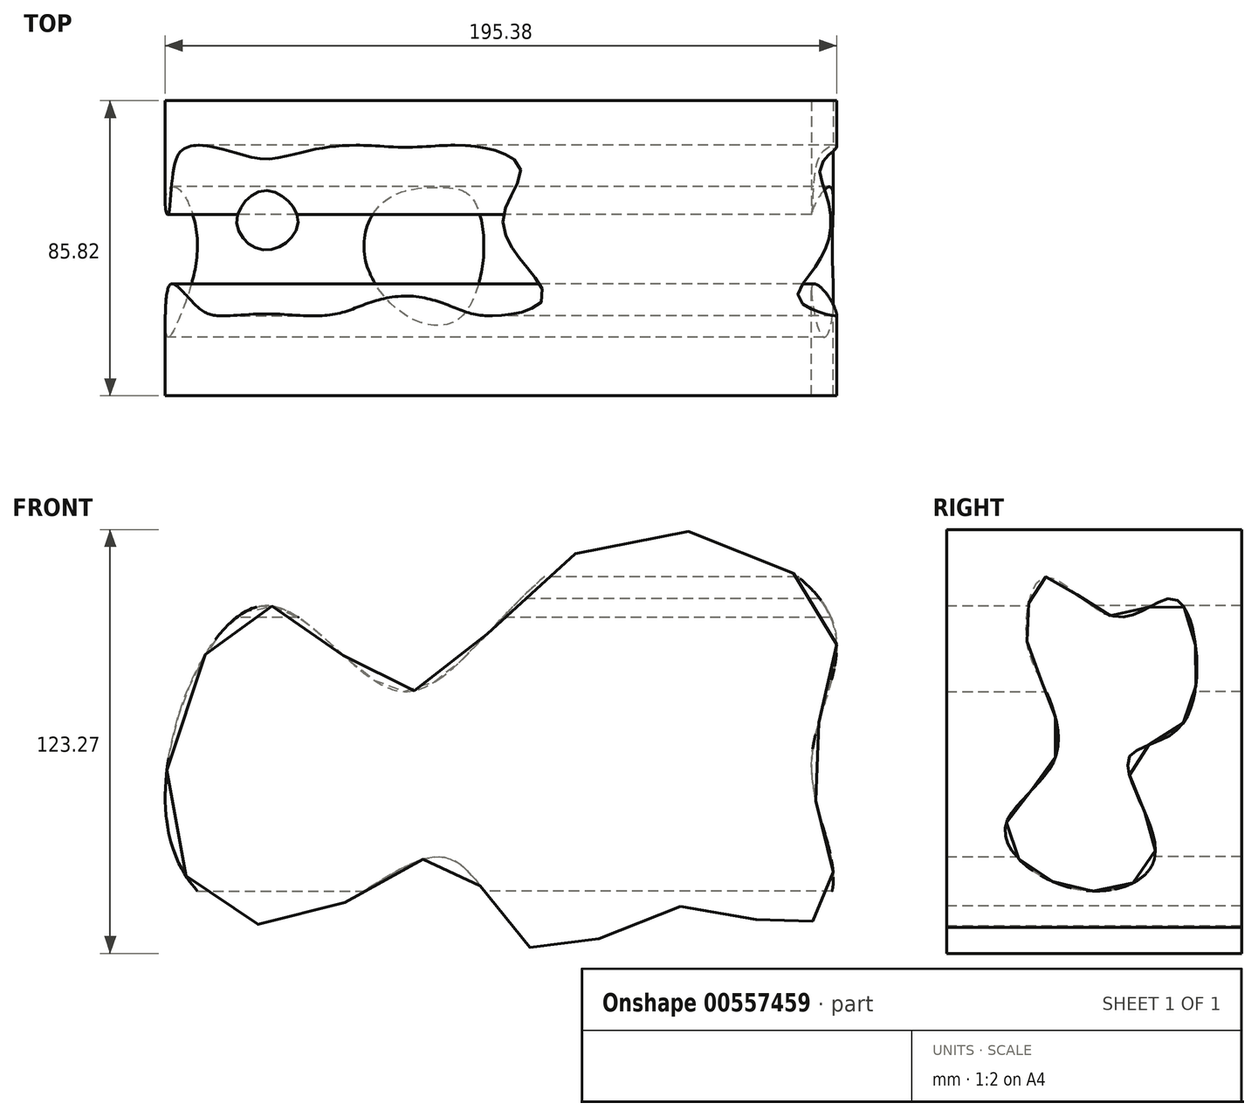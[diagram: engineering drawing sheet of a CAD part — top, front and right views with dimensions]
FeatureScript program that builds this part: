
annotation { "Feature Type Name" : "Feature", "Feature Type Description" : "" }
export const myFeature = defineFeature(function(context is Context, id is Id, definition is map)
    precondition{}
    {
        {
            var Q0;
            Q0=qCreatedBy(makeId("Front.planeOp"),FACE);
            var sketch = newSketch(context, id + "F0", { "sketchPlane" : qUnion([Q0])});
            skFitSpline(sketch, "E0", {"points": [v(67.5, -42.82) * mm, v(25.95, -55.78) * mm, v(0, -28.79) * mm, v(-44.79, -47.76) * mm, v(-81.65, -19.98) * mm, v(-53.57, 44.65) * mm, v(-13.21, 19.74) * mm, v(44.9, 63.82) * mm, v(111.38, 41.25) * mm, v(105.73, 0) * mm, v(112.03, -36) * mm, v(101.22, -48.79) * mm, v(67.5, -42.82) * mm]});
            skSolve(sketch);
        }
        {
            var Q0;
            Q0=makeQuery(id+"F0.imprint","IMPRINT",FACE,{"disambiguationData":[TD([[makeQuery(id+"F0.imprint","IMPRINT",EDGE,{"derivedFrom":sQuery(id+"F0.wireOp",EDGE,"E0")}),-1.0]])]});
            extrude(context, id + "F1", {"entities" : qUnion([Q0]), "oppositeDirection" : true, "depth" : 85.82 * mm, "offsetDistance" : 25.4 * mm});
        }
        {
            var Q0;
            Q0=qCreatedBy(makeId("Right.planeOp"),FACE);
            cPlane(context, id + "F2", {"entities" : qUnion([Q0]), "cplaneType" : CPlaneType.OFFSET, "offset" : 124.9 * mm, "width" : 152.4 * mm, "height" : 152.4 * mm});
        }
        {
            var Q0;
            Q0=qCreatedBy(id+"F2.planeOp",FACE);
            var sketch = newSketch(context, id + "F3", { "sketchPlane" : qUnion([Q0])});
            skFitSpline(sketch, "E1", {"points": [v(27.42, 23.08) * mm, v(23.22, 36.58) * mm, v(28.68, 53.05) * mm, v(50.04, 41.35) * mm, v(66.96, 46.36) * mm, v(68.92, 10.62) * mm, v(52.9, 0) * mm, v(60.7, -27.76) * mm, v(38.6, -37.9) * mm, v(17, -20.43) * mm, v(31.45, 0) * mm, v(27.42, 23.08) * mm]});
            skSolve(sketch);
        }
        {
            var Q0;
            Q0=makeQuery(id+"F3.imprint","IMPRINT",FACE,{"disambiguationData":[TD([[makeQuery(id+"F3.imprint","IMPRINT",EDGE,{"derivedFrom":sQuery(id+"F3.wireOp",EDGE,"E1")}),-1.0]])]});
            extrude(context, id + "F4", {"entities" : qUnion([Q0]), "operationType" : NewBodyOperationType.REMOVE, "oppositeDirection" : true, "depth" : 261.58 * mm, "offsetDistance" : 25.4 * mm});
        }
    });
